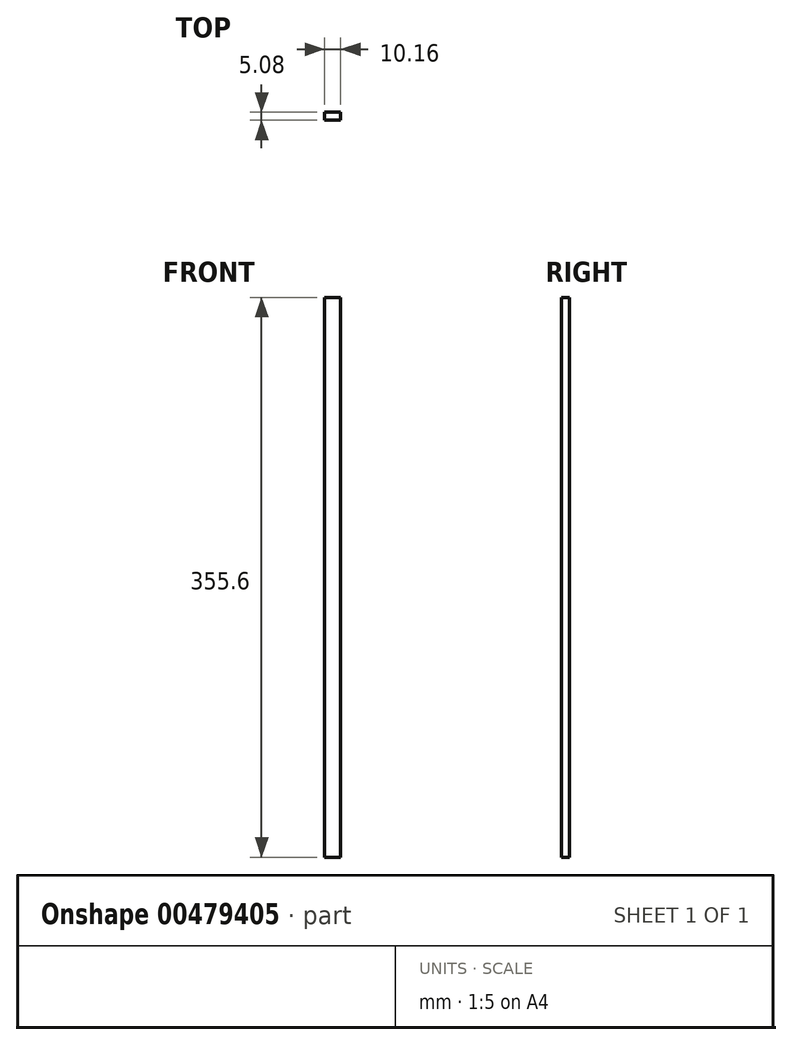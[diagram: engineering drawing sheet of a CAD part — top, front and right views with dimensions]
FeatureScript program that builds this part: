
annotation { "Feature Type Name" : "Feature", "Feature Type Description" : "" }
export const myFeature = defineFeature(function(context is Context, id is Id, definition is map)
    precondition{}
    {
        {
            var Q0;
            Q0=qCreatedBy(makeId("Top.planeOp"),FACE);
            var sketch = newSketch(context, id + "F0", { "sketchPlane" : qUnion([Q0])});
            skLineSegment(sketch, "E0.bottom", {"start": v(0, 0) * mm, "end": v(10.16, 0) * mm});
            skLineSegment(sketch, "E0.top", {"start": v(0, 5.08) * mm, "end": v(10.16, 5.08) * mm});
            skLineSegment(sketch, "E0.left", {"start": v(0, 0) * mm, "end": v(0, 5.08) * mm});
            skLineSegment(sketch, "E0.right", {"start": v(10.16, 0) * mm, "end": v(10.16, 5.08) * mm});
            skSolve(sketch);
        }
        {
            var Q0;
            Q0 = qSketchRegion(id + "F0", true);
            extrude(context, id + "F1", {"entities" : qUnion([Q0]), "depth" : 355.6 * mm, "offsetDistance" : 25.4 * mm});
        }
    });
